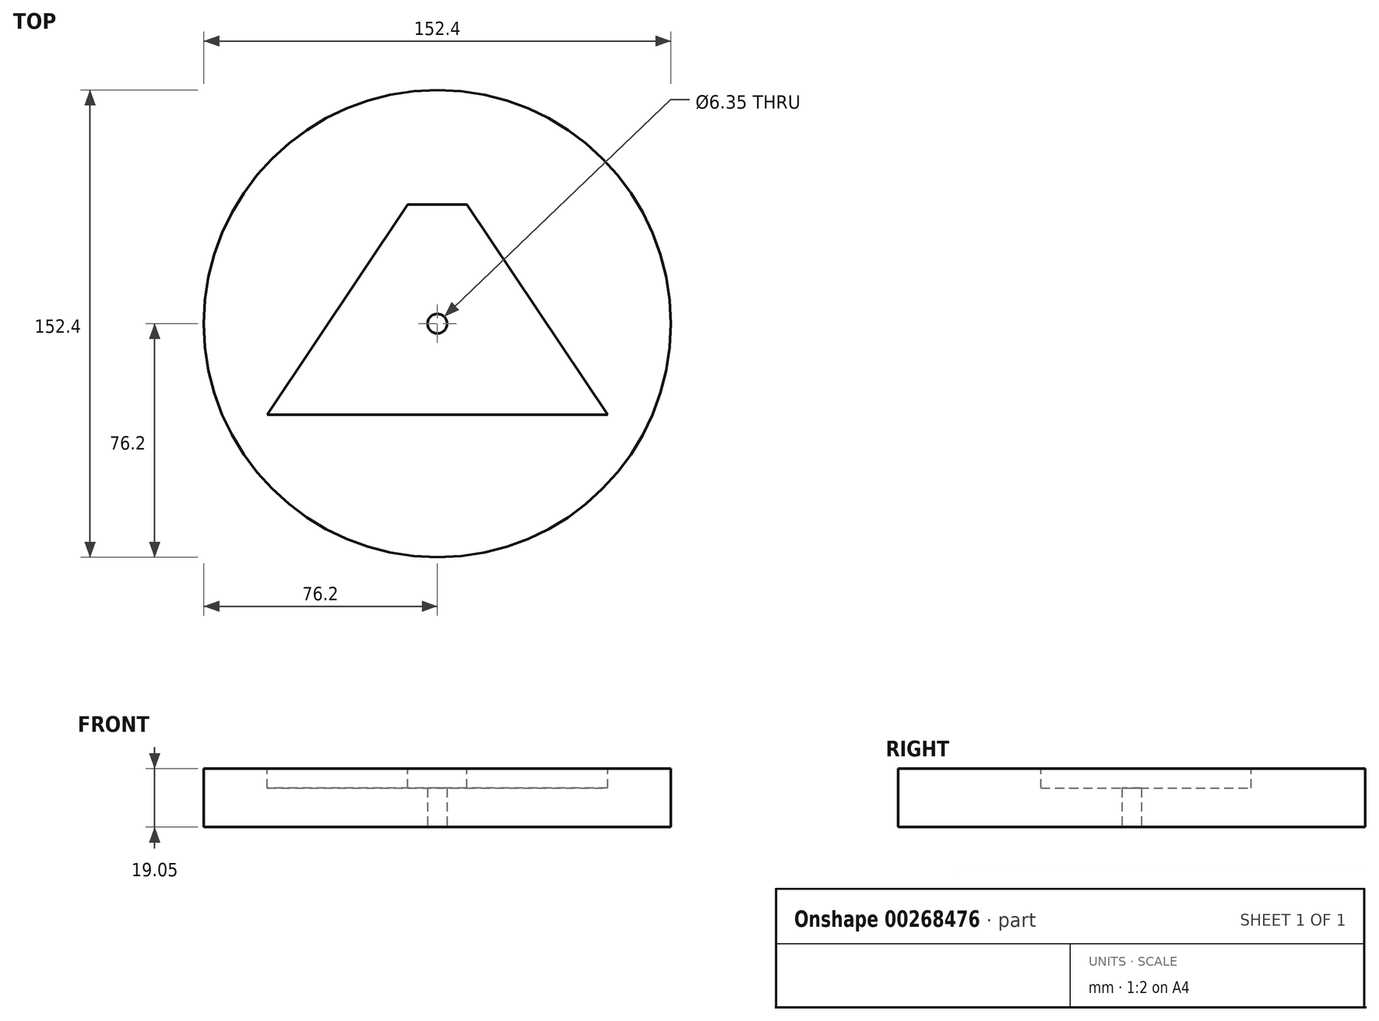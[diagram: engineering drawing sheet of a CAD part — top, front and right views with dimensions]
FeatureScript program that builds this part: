
annotation { "Feature Type Name" : "Feature", "Feature Type Description" : "" }
export const myFeature = defineFeature(function(context is Context, id is Id, definition is map)
    precondition{}
    {
        {
            var Q0;
            Q0=qCreatedBy(makeId("Top.planeOp"),FACE);
            var sketch = newSketch(context, id + "F0", { "sketchPlane" : qUnion([Q0])});
            skCircle(sketch, "E0", {"center": v(0, 0) * mm, "radius": 76.2 * mm});
            skCircle(sketch, "E1", {"center": v(0, 0) * mm, "radius": 3.18 * mm});
            skSolve(sketch);
        }
        {
            var Q0;
            Q0=qSketchRegion(id+"F0",true);
            extrude(context, id + "F1", {"entities" : qUnion([Q0]), "depth" : 19.05 * mm});
        }
        {
            var Q0;
            Q0=makeQuery(id+"F1.opExtrude","CAP_FACE",FACE,{"disambiguationData":[OSD([sQuery(id+"F0.wireOp",EDGE,"E0"),sQuery(id+"F0.wireOp",EDGE,"E1")])],"isStart":false});
            var sketch = newSketch(context, id + "F2", { "sketchPlane" : qUnion([Q0])});
            skLineSegment(sketch, "E2", {"start": v(-9.65, 38.93) * mm, "end": v(9.65, 38.93) * mm});
            skLineSegment(sketch, "E3", {"start": v(9.65, 38.93) * mm, "end": v(55.56, -29.68) * mm});
            skLineSegment(sketch, "E4", {"start": v(55.56, -29.68) * mm, "end": v(-55.56, -29.68) * mm});
            skLineSegment(sketch, "E5", {"start": v(-55.56, -29.68) * mm, "end": v(-9.65, 38.93) * mm});
            skSolve(sketch);
        }
        {
            var Q0;
            Q0=qSketchRegion(id+"F2",true);
            extrude(context, id + "F3", {"entities" : qUnion([Q0]), "operationType" : NewBodyOperationType.REMOVE, "oppositeDirection" : true, "depth" : 6.35 * mm});
        }
    });
